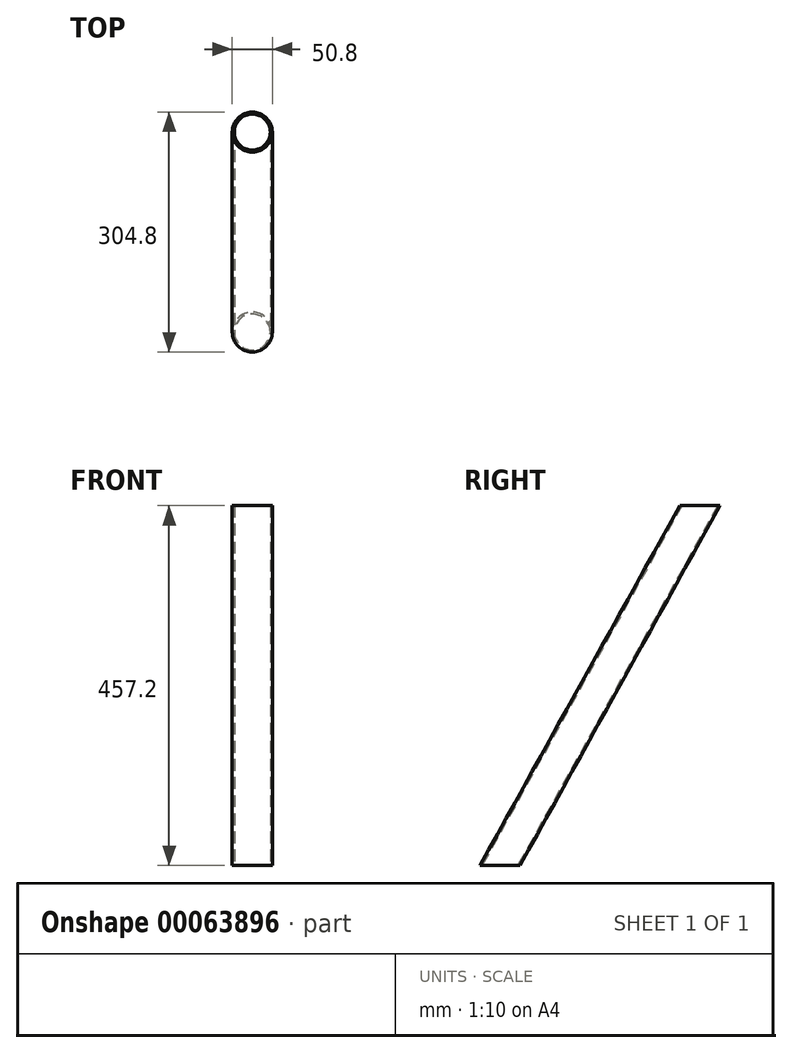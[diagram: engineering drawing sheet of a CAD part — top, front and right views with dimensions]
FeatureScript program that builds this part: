
annotation { "Feature Type Name" : "Feature", "Feature Type Description" : "" }
export const myFeature = defineFeature(function(context is Context, id is Id, definition is map)
    precondition{}
    {
        {
            var Q0;
            Q0=qCreatedBy(makeId("Top.planeOp"),FACE);
            var sketch = newSketch(context, id + "F0", { "sketchPlane" : qUnion([Q0])});
            skCircle(sketch, "E0", {"center": v(0, 0) * mm, "radius": 25.4 * mm});
            skCircle(sketch, "E1", {"center": v(0, 0) * mm, "radius": 22.86 * mm});
            skSolve(sketch);
        }
        {
            var Q0;
            Q0=qCreatedBy(makeId("Right.planeOp"),FACE);
            var sketch = newSketch(context, id + "F1", { "sketchPlane" : qUnion([Q0])});
            skLineSegment(sketch, "E2", {"start": v(0, 0) * mm, "end": v(0, 457.2) * mm, "construction": true});
            skLineSegment(sketch, "E3", {"start": v(0, 0) * mm, "end": v(254, 457.2) * mm});
            skLineSegment(sketch, "E4", {"start": v(0, 457.2) * mm, "end": v(254, 457.2) * mm, "construction": true});
            skSolve(sketch);
        }
        {
            var Q0;
            Q0=makeQuery(id+"F0.imprint","IMPRINT",FACE,{"disambiguationData":[TD([[makeQuery(id+"F0.imprint","IMPRINT",EDGE,{"derivedFrom":sQuery(id+"F0.wireOp",EDGE,"E0")}),1.0]])]});
            var Q1;
            Q1=sQuery(id+"F0.wireOp",EDGE,"E0");
            var Q2;
            Q2=sQuery(id+"F1.wireOp",EDGE,"E3");
            sweep(context, id + "F2", {"profiles" : qUnion([Q0]), "surfaceProfiles" : qUnion([Q1]), "path" : qUnion([Q2])});
        }
    });
